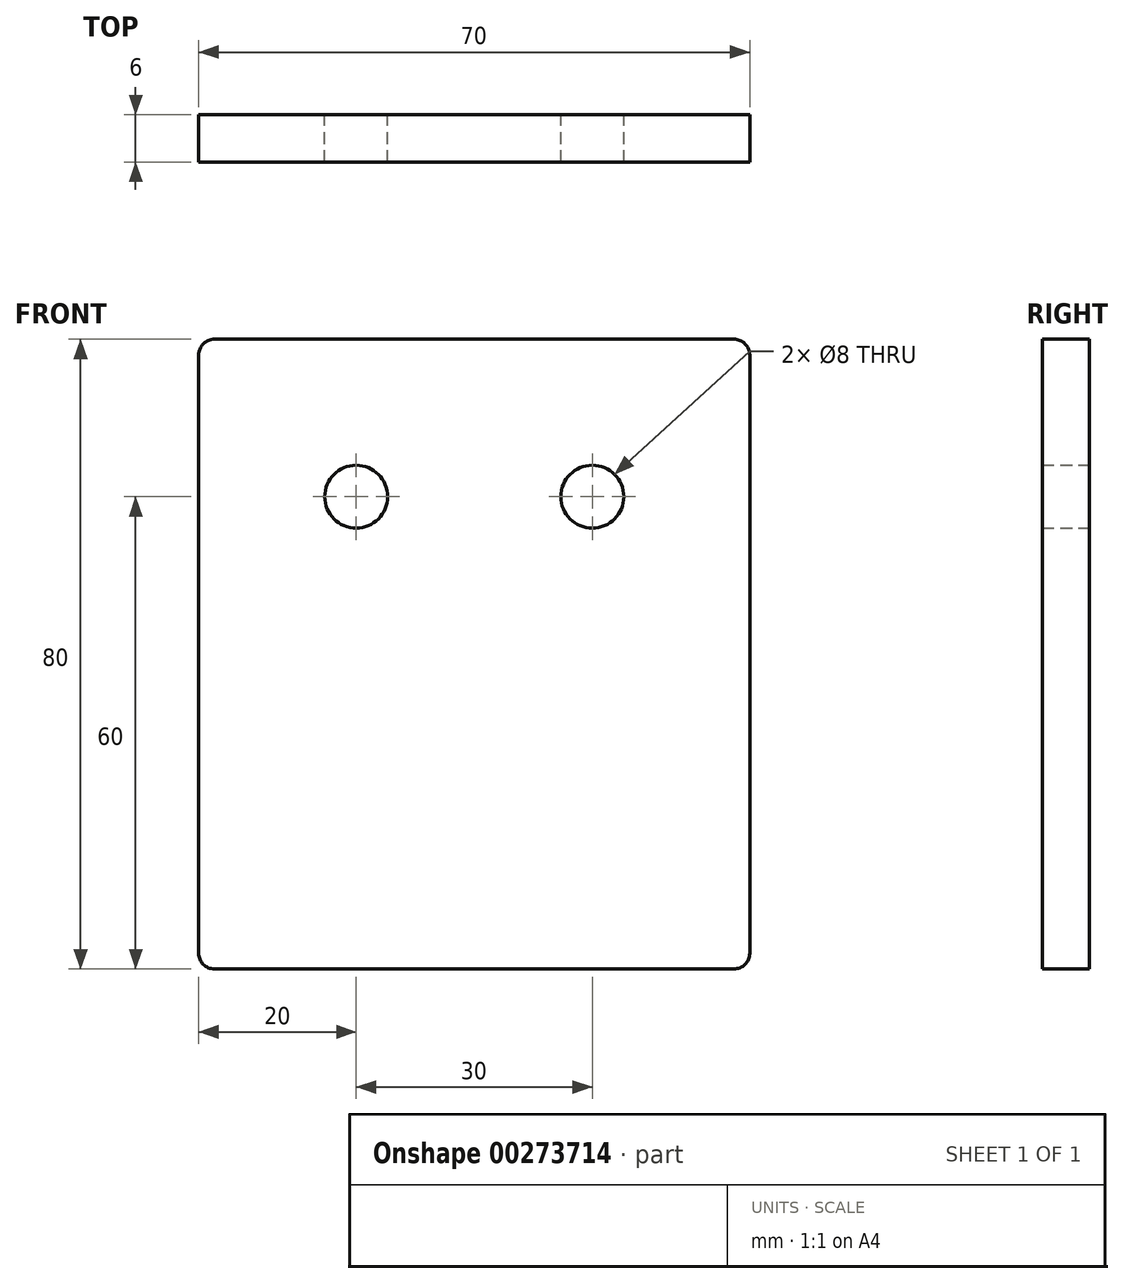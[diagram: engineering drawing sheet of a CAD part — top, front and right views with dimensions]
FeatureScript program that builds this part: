
annotation { "Feature Type Name" : "Feature", "Feature Type Description" : "" }
export const myFeature = defineFeature(function(context is Context, id is Id, definition is map)
    precondition{}
    {
        {
            var Q0;
            Q0=qCreatedBy(makeId("Front.planeOp"),FACE);
            var sketch = newSketch(context, id + "F0", { "sketchPlane" : qUnion([Q0])});
            skLineSegment(sketch, "E0.bottom", {"start": v(33, 40) * mm, "end": v(-33, 40) * mm});
            skLineSegment(sketch, "E0.top", {"start": v(33, -40) * mm, "end": v(-33, -40) * mm});
            skLineSegment(sketch, "E0.left", {"start": v(35, 38) * mm, "end": v(35, -38) * mm});
            skLineSegment(sketch, "E0.right", {"start": v(-35, 38) * mm, "end": v(-35, -38) * mm});
            skPoint(sketch, "E0.middle", {"position": v(0, 0) * mm});
            skPoint(sketch, "E1.visualSharp", {"position": v(-35, 40) * mm});
            skArc(sketch, "E1.filletArc", {"start": v(-33, 40) * mm, "mid": v(-34.41, 39.41) * mm, "end": v(-35, 38) * mm});
            skPoint(sketch, "E2.visualSharp", {"position": v(35, 40) * mm});
            skArc(sketch, "E2.filletArc", {"start": v(35, 38) * mm, "mid": v(34.41, 39.41) * mm, "end": v(33, 40) * mm});
            skPoint(sketch, "E3.visualSharp", {"position": v(35, -40) * mm});
            skArc(sketch, "E3.filletArc", {"start": v(33, -40) * mm, "mid": v(34.41, -39.41) * mm, "end": v(35, -38) * mm});
            skPoint(sketch, "E4.visualSharp", {"position": v(-35, -40) * mm});
            skArc(sketch, "E4.filletArc", {"start": v(-35, -38) * mm, "mid": v(-34.41, -39.41) * mm, "end": v(-33, -40) * mm});
            skPoint(sketch, "E5", {"position": v(-15, 20) * mm});
            skPoint(sketch, "E6", {"position": v(15, 20) * mm});
            skCircle(sketch, "E7", {"center": v(-15, 20) * mm, "radius": 4 * mm});
            skCircle(sketch, "E8", {"center": v(15, 20) * mm, "radius": 4 * mm});
            skSolve(sketch);
        }
        {
            var Q0;
            Q0=makeQuery(id+"F0.imprint","IMPRINT",FACE,{"disambiguationData":[TD([[makeQuery(id+"F0.imprint","IMPRINT",EDGE,{"derivedFrom":sQuery(id+"F0.wireOp",EDGE,"E0.bottom")}),1.0]])]});
            extrude(context, id + "F1", {"entities" : qUnion([Q0]), "depth" : 6 * mm});
        }
    });
